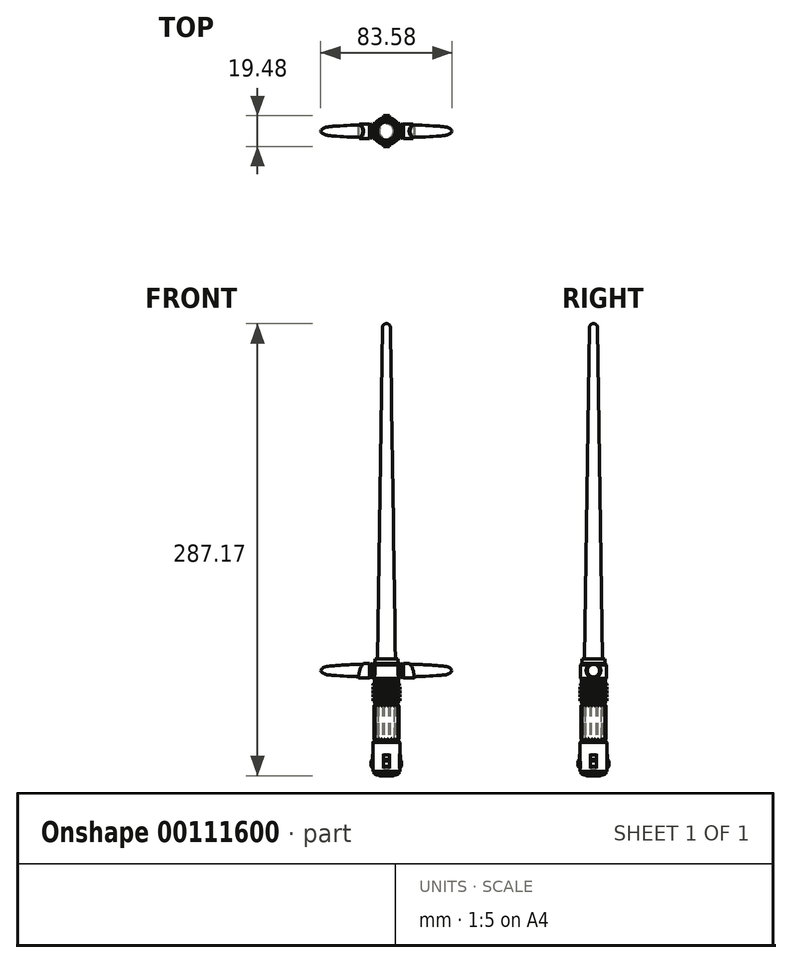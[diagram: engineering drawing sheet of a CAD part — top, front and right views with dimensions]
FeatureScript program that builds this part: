
annotation { "Feature Type Name" : "Feature", "Feature Type Description" : "" }
export const myFeature = defineFeature(function(context is Context, id is Id, definition is map)
    precondition{}
    {
        {
            var Q0;
            Q0=qCreatedBy(makeId("Front.planeOp"),FACE);
            var sketch = newSketch(context, id + "F0", { "sketchPlane" : qUnion([Q0])});
            skLineSegment(sketch, "E0", {"start": v(0, 37) * mm, "end": v(7.3, 37) * mm});
            skLineSegment(sketch, "E1", {"start": v(7.3, 37) * mm, "end": v(7.35, 34.29) * mm});
            skLineSegment(sketch, "E2", {"start": v(7.35, 34.29) * mm, "end": v(8.24, 33.16) * mm});
            skLineSegment(sketch, "E3", {"start": v(8.24, 33.16) * mm, "end": v(8.24, 24.6) * mm});
            skLineSegment(sketch, "E4", {"start": v(8.24, 24.6) * mm, "end": v(7.65, 23.84) * mm});
            skLineSegment(sketch, "E5", {"start": v(7.65, 23.84) * mm, "end": v(7.65, 21.71) * mm});
            skLineSegment(sketch, "E6", {"start": v(7.65, 21.71) * mm, "end": v(8.41, 21.12) * mm});
            skLineSegment(sketch, "E7", {"start": v(8.41, 21.12) * mm, "end": v(8.41, 20.12) * mm});
            skLineSegment(sketch, "E8", {"start": v(8.41, 20.12) * mm, "end": v(7.59, 20.12) * mm});
            skLineSegment(sketch, "E9", {"start": v(7.59, 20.12) * mm, "end": v(7.59, 19.18) * mm});
            skLineSegment(sketch, "E10", {"start": v(7.59, 19.18) * mm, "end": v(8.49, 19.18) * mm});
            skLineSegment(sketch, "E11", {"start": v(8.49, 19.18) * mm, "end": v(8.49, 17.5) * mm});
            skLineSegment(sketch, "E12", {"start": v(8.49, 17.5) * mm, "end": v(7.52, 17.5) * mm});
            skLineSegment(sketch, "E13", {"start": v(7.52, 17.5) * mm, "end": v(7.52, 16.91) * mm});
            skLineSegment(sketch, "E14", {"start": v(7.52, 16.91) * mm, "end": v(8.5, 16.91) * mm});
            skLineSegment(sketch, "E15", {"start": v(8.5, 16.91) * mm, "end": v(8.5, 15.12) * mm});
            skLineSegment(sketch, "E16", {"start": v(8.5, 15.12) * mm, "end": v(7.53, 15.12) * mm});
            skLineSegment(sketch, "E17", {"start": v(7.53, 15.12) * mm, "end": v(7.53, 14.37) * mm});
            skLineSegment(sketch, "E18", {"start": v(7.53, 14.37) * mm, "end": v(8.5, 14.37) * mm});
            skLineSegment(sketch, "E19", {"start": v(8.5, 14.37) * mm, "end": v(8.5, 12.85) * mm});
            skLineSegment(sketch, "E20", {"start": v(8.5, 12.85) * mm, "end": v(7.56, 12.85) * mm});
            skLineSegment(sketch, "E21", {"start": v(7.56, 12.85) * mm, "end": v(7.56, 11.91) * mm});
            skLineSegment(sketch, "E22", {"start": v(7.56, 11.91) * mm, "end": v(8.49, 11.91) * mm});
            skLineSegment(sketch, "E23", {"start": v(8.49, 11.91) * mm, "end": v(8.49, 10.4) * mm});
            skLineSegment(sketch, "E24", {"start": v(8.49, 10.4) * mm, "end": v(7.62, 10.4) * mm});
            skLineSegment(sketch, "E25", {"start": v(7.62, 10.4) * mm, "end": v(7.62, 9) * mm});
            skLineSegment(sketch, "E26", {"start": v(7.62, 9) * mm, "end": v(6.87, 9) * mm});
            skLineSegment(sketch, "E27", {"start": v(6.87, 9) * mm, "end": v(6.87, 8.81) * mm});
            skLineSegment(sketch, "E28", {"start": v(6.87, 8.81) * mm, "end": v(7.19, 8.81) * mm});
            skLineSegment(sketch, "E29", {"start": v(7.19, 8.81) * mm, "end": v(7.19, 8.55) * mm});
            skLineSegment(sketch, "E30", {"start": v(7.19, 8.55) * mm, "end": v(7.37, 8.55) * mm});
            skLineSegment(sketch, "E31", {"start": v(7.37, 8.55) * mm, "end": v(7.37, 7.87) * mm});
            skLineSegment(sketch, "E32", {"start": v(7.37, 7.87) * mm, "end": v(7.56, 7.87) * mm});
            skLineSegment(sketch, "E33", {"start": v(7.56, 7.87) * mm, "end": v(7.56, -14.92) * mm});
            skLineSegment(sketch, "E34", {"start": v(7.56, -14.92) * mm, "end": v(8.66, -16.09) * mm});
            skLineSegment(sketch, "E35", {"start": v(8.66, -16.09) * mm, "end": v(8.66, -23.38) * mm});
            skLineSegment(sketch, "E36", {"start": v(8.6, -32.9) * mm, "end": v(8.6, -34.53) * mm});
            skLineSegment(sketch, "E37", {"start": v(8.6, -34.53) * mm, "end": v(8.02, -34.53) * mm});
            skLineSegment(sketch, "E38", {"start": v(8.02, -34.53) * mm, "end": v(8.02, -35.87) * mm});
            skLineSegment(sketch, "E39", {"start": v(8.02, -35.87) * mm, "end": v(7.3, -35.87) * mm});
            skLineSegment(sketch, "E40", {"start": v(7.3, -35.87) * mm, "end": v(7.3, -36.2) * mm});
            skLineSegment(sketch, "E41", {"start": v(7.3, -36.2) * mm, "end": v(6.77, -36.2) * mm});
            skLineSegment(sketch, "E42", {"start": v(6.77, -36.2) * mm, "end": v(6.77, -36.42) * mm});
            skLineSegment(sketch, "E43", {"start": v(6.77, -36.42) * mm, "end": v(6.4, -36.42) * mm});
            skLineSegment(sketch, "E44", {"start": v(6.4, -36.42) * mm, "end": v(6.4, -36.76) * mm});
            skLineSegment(sketch, "E45", {"start": v(6.4, -36.76) * mm, "end": v(5.1, -36.76) * mm});
            skLineSegment(sketch, "E46", {"start": v(5.1, -36.76) * mm, "end": v(5.1, -36.92) * mm});
            skLineSegment(sketch, "E47", {"start": v(5.1, -36.92) * mm, "end": v(4.54, -36.92) * mm});
            skLineSegment(sketch, "E48", {"start": v(4.54, -36.92) * mm, "end": v(4.54, -37.17) * mm});
            skLineSegment(sketch, "E49", {"start": v(4.54, -37.17) * mm, "end": v(0, -37.17) * mm});
            skLineSegment(sketch, "E50", {"start": v(0, -37.17) * mm, "end": v(0, 37) * mm});
            skLineSegment(sketch, "E51", {"start": v(8.66, -23.38) * mm, "end": v(8.6, -32.9) * mm});
            skLineSegment(sketch, "E52", {"start": v(7.56, 7.87) * mm, "end": v(8.1, 7.39) * mm});
            skLineSegment(sketch, "E53", {"start": v(8.1, 7.39) * mm, "end": v(8.1, -14.41) * mm});
            skLineSegment(sketch, "E54", {"start": v(8.1, -14.41) * mm, "end": v(6.71, -14.41) * mm});
            skLineSegment(sketch, "E55", {"start": v(6.71, -14.41) * mm, "end": v(6.71, 7.86) * mm});
            skLineSegment(sketch, "E56", {"start": v(6.71, 7.86) * mm, "end": v(7.56, 7.87) * mm});
            skLineSegment(sketch, "E57", {"start": v(8.66, -23.38) * mm, "end": v(9.19, -24.01) * mm});
            skLineSegment(sketch, "E58", {"start": v(9.19, -24.01) * mm, "end": v(9.19, -26.92) * mm});
            skLineSegment(sketch, "E59", {"start": v(9.19, -26.92) * mm, "end": v(9.94, -27.8) * mm});
            skLineSegment(sketch, "E60", {"start": v(9.94, -27.8) * mm, "end": v(9.94, -31.32) * mm});
            skLineSegment(sketch, "E61", {"start": v(9.94, -31.32) * mm, "end": v(8.6, -32.4) * mm});
            skLineSegment(sketch, "E62", {"start": v(8.6, -32.4) * mm, "end": v(7.88, -32.4) * mm});
            skLineSegment(sketch, "E63", {"start": v(7.88, -32.4) * mm, "end": v(7.88, -23.67) * mm});
            skLineSegment(sketch, "E64", {"start": v(8.66, -23.38) * mm, "end": v(7.88, -23.38) * mm});
            skLineSegment(sketch, "E65", {"start": v(7.88, -23.38) * mm, "end": v(7.88, -23.67) * mm});
            skLineSegment(sketch, "E66", {"start": v(7.02, 33.16) * mm, "end": v(8.24, 33.16) * mm});
            skLineSegment(sketch, "E67", {"start": v(8.24, 33.16) * mm, "end": v(8.24, 34.28) * mm});
            skLineSegment(sketch, "E68", {"start": v(8.24, 34.28) * mm, "end": v(9.65, 34.28) * mm});
            skLineSegment(sketch, "E69", {"start": v(9.65, 34.28) * mm, "end": v(9.63, 33.97) * mm});
            skLineSegment(sketch, "E70", {"start": v(11.77, 34.18) * mm, "end": v(18.79, 34.18) * mm});
            skLineSegment(sketch, "E71", {"start": v(18.79, 34.18) * mm, "end": v(18.79, 29.6) * mm});
            skLineSegment(sketch, "E72", {"start": v(18.79, 29.6) * mm, "end": v(7.02, 29.6) * mm});
            skLineSegment(sketch, "E73", {"start": v(7.02, 29.6) * mm, "end": v(7.02, 33.16) * mm});
            skLineSegment(sketch, "E74", {"start": v(9.63, 33.97) * mm, "end": v(9.63, 33.3) * mm});
            skLineSegment(sketch, "E75", {"start": v(9.63, 33.3) * mm, "end": v(9.96, 33.3) * mm});
            skLineSegment(sketch, "E76", {"start": v(9.96, 33.3) * mm, "end": v(10.32, 33.78) * mm});
            skLineSegment(sketch, "E77", {"start": v(11.02, 33.88) * mm, "end": v(11.36, 33.63) * mm});
            skLineSegment(sketch, "E78", {"start": v(11.36, 33.63) * mm, "end": v(11.77, 34.18) * mm});
            skPoint(sketch, "E79.visualSharp", {"position": v(10.62, 34.18) * mm});
            skArc(sketch, "E79.filletArc", {"start": v(11.02, 33.88) * mm, "mid": v(10.65, 33.98) * mm, "end": v(10.32, 33.78) * mm});
            skPoint(sketch, "E80.endSnap0", {"position": v(12.9, 29.6) * mm});
            skLineSegment(sketch, "E81", {"start": v(48.79, 29.6) * mm, "end": v(18.79, 29.6) * mm});
            skPoint(sketch, "E82.3.internal.snap0", {"position": v(18.79, 31.9) * mm});
            skFitSpline(sketch, "E83", {"points": [v(15.28, 34.18) * mm, v(18.79, 33.79) * mm, v(29.96, 33.34) * mm, v(40.36, 32.7) * mm, v(46.93, 31.51) * mm, v(48.79, 29.6) * mm], "startDerivative": vector(18.62, -2.48) * mm, "endDerivative": vector(9.66, -15.82) * mm});
            skSolve(sketch);
        }
        {
            var Q0;
            Q0=makeQuery(id+"F0.imprint","IMPRINT",FACE,{"disambiguationData":[TD([[makeQuery(id+"F0.imprint","IMPRINT",EDGE,{"derivedFrom":sQuery(id+"F0.wireOp",EDGE,"E0")}),-1.0]])]});
            var Q1;
            {var subQ0=sQuery(id+"F0.wireOp",EDGE,"E66");Q1=makeQuery(id+"F0.imprint","IMPRINT",FACE,{"disambiguationData":[TD([[makeQuery(id+"F0.imprint","IMPRINT",EDGE,{"derivedFrom":subQ0}),-1.0]])]});}
            var Q2;
            {var subQ4=sQuery(id+"F0.wireOp",EDGE,"E55");Q2=makeQuery(id+"F0.imprint","IMPRINT",FACE,{"disambiguationData":[TD([[makeQuery(id+"F0.imprint","IMPRINT",EDGE,{"derivedFrom":subQ4}),-1.0]])]});}
            var Q3;
            {var subQ1=sQuery(id+"F0.wireOp",EDGE,"E62");Q3=makeQuery(id+"F0.imprint","IMPRINT",FACE,{"disambiguationData":[TD([[makeQuery(id+"F0.imprint","IMPRINT",EDGE,{"derivedFrom":subQ1}),-1.0]])]});}
            var Q4;
            Q4=sQuery(id+"F0.wireOp",EDGE,"E50");
            revolve(context, id + "F1", {"entities" : qUnion([Q0, Q1, Q2, Q3]), "axis" : qUnion([Q4]), "revolveType" : RevolveType.FULL});
        }
        {
            var Q0;
            {var subQ10=sQuery(id+"F0.wireOp",EDGE,"E67");Q0=makeQuery(id+"F0.imprint","IMPRINT",FACE,{"disambiguationData":[TD([[makeQuery(id+"F0.imprint","IMPRINT",EDGE,{"derivedFrom":subQ10}),-1.0]])]});}
            var Q1;
            {var subQ0=sQuery(id+"F0.wireOp",EDGE,"E71");var subQ1=sQuery(id+"F0.wireOp",EDGE,"E70");var subQ2=makeQuery(id+"F0.imprint","INTERSECT",VERTEX,{"derivedFrom":[subQ1,subQ0]});Q1=makeQuery(id+"F0.imprint","IMPRINT",FACE,{"disambiguationData":[TD([[makeQuery(id+"F0.imprint","IMPRINT",EDGE,{"disambiguationData":[TD([[subQ2,1.0]])],"derivedFrom":subQ1}),-1.0]])]});}
            var Q2;
            Q2=sQuery(id+"F0.wireOp",EDGE,"E72");
            revolve(context, id + "F2", {"entities" : qUnion([Q0, Q1]), "axis" : qUnion([Q2]), "revolveType" : RevolveType.FULL});
        }
        {
            var Q0;
            {var subQ0=sQuery(id+"F0.wireOp",EDGE,"E52");Q0=makeQuery(id+"F0.imprint","IMPRINT",FACE,{"disambiguationData":[TD([[makeQuery(id+"F0.imprint","IMPRINT",EDGE,{"derivedFrom":subQ0}),-1.0]])]});}
            extrude(context, id + "F3", {"entities" : qUnion([Q0]), "endBound" : BoundingType.SYMMETRIC, "depth" : 3 * mm});
        }
        {
            var Q0;
            {var subQ0=sQuery(id+"F0.wireOp",EDGE,"E57");Q0=makeQuery(id+"F0.imprint","IMPRINT",FACE,{"disambiguationData":[TD([[makeQuery(id+"F0.imprint","IMPRINT",EDGE,{"derivedFrom":subQ0}),-1.0]])]});}
            extrude(context, id + "F4", {"entities" : qUnion([Q0]), "endBound" : BoundingType.SYMMETRIC, "depth" : 4 * mm});
        }
        {
            var Q0;
            Q0=makeQuery(id+"F2.opRevolve","SWEPT_BODY",BODY,{"disambiguationData":[OSD([sQuery(id+"F0.wireOp",EDGE,"E3"),sQuery(id+"F0.wireOp",EDGE,"E67"),sQuery(id+"F0.wireOp",EDGE,"E68"),sQuery(id+"F0.wireOp",EDGE,"E69"),sQuery(id+"F0.wireOp",EDGE,"E70"),sQuery(id+"F0.wireOp",EDGE,"E71"),sQuery(id+"F0.wireOp",EDGE,"E72"),sQuery(id+"F0.wireOp",EDGE,"E74"),sQuery(id+"F0.wireOp",EDGE,"E75"),sQuery(id+"F0.wireOp",EDGE,"E76")])]});
            var Q1;
            Q1=sQuery(id+"F0.wireOp",EDGE,"E72");
            var Q2;
            Q2=sQuery(id+"F0.wireOp",EDGE,"E72");
            transform(context, id + "F5", {"entities" : qUnion([Q0]), "transformType" : TransformType.TRANSLATION_DISTANCE, "transformDirection" : qUnion([Q2]), "distance" : 1 * mm, "makeCopy" : false});
        }
        {
            var Q0;
            Q0=makeQuery(id+"F3.opExtrude","SWEPT_BODY",BODY,{"disambiguationData":[OSD([sQuery(id+"F0.wireOp",EDGE,"E33"),sQuery(id+"F0.wireOp",EDGE,"E52"),sQuery(id+"F0.wireOp",EDGE,"E53"),sQuery(id+"F0.wireOp",EDGE,"E54")])]});
            var Q1;
            Q1=sQuery(id+"F0.wireOp",EDGE,"E54");
            var Q2;
            Q2=sQuery(id+"F0.wireOp",EDGE,"E54");
            transform(context, id + "F6", {"entities" : qUnion([Q0]), "transformType" : TransformType.TRANSLATION_DISTANCE, "transformDirection" : qUnion([Q2]), "distance" : 0.2 * mm, "makeCopy" : false});
        }
        {
            var Q0;
            Q0=makeQuery(id+"F4.opExtrude","SWEPT_BODY",BODY,{"disambiguationData":[OSD([sQuery(id+"F0.wireOp",EDGE,"E51"),sQuery(id+"F0.wireOp",EDGE,"E57"),sQuery(id+"F0.wireOp",EDGE,"E58"),sQuery(id+"F0.wireOp",EDGE,"E59"),sQuery(id+"F0.wireOp",EDGE,"E60"),sQuery(id+"F0.wireOp",EDGE,"E61")])]});
            var Q1;
            Q1=sQuery(id+"F0.wireOp",EDGE,"E54");
            transform(context, id + "F7", {"entities" : qUnion([Q0]), "transformType" : TransformType.TRANSLATION_DISTANCE, "transformDirection" : qUnion([Q1]), "distance" : 0.2 * mm, "makeCopy" : false});
        }
        {
            var Q0;
            Q0=makeQuery(id+"F2.opRevolve","SWEPT_BODY",BODY,{"disambiguationData":[OSD([sQuery(id+"F0.wireOp",EDGE,"E3"),sQuery(id+"F0.wireOp",EDGE,"E67"),sQuery(id+"F0.wireOp",EDGE,"E68"),sQuery(id+"F0.wireOp",EDGE,"E69"),sQuery(id+"F0.wireOp",EDGE,"E70"),sQuery(id+"F0.wireOp",EDGE,"E71"),sQuery(id+"F0.wireOp",EDGE,"E72"),sQuery(id+"F0.wireOp",EDGE,"E74"),sQuery(id+"F0.wireOp",EDGE,"E75"),sQuery(id+"F0.wireOp",EDGE,"E76")])]});
            var Q1;
            Q1=qCreatedBy(makeId("Right.planeOp"),FACE);
            mirror(context, id + "F8", {"operationType" : NewBodyOperationType.ADD, "entities" : qUnion([Q0]), "mirrorPlane" : qUnion([Q1])});
        }
        {
            var Q0;
            Q0=makeQuery(id+"F3.opExtrude","SWEPT_FACE",FACE,{"disambiguationData":[OSD([sQuery(id+"F0.wireOp",EDGE,"E53")])]});
            fillet(context, id + "F9", {"entities" : qUnion([Q0]), "radius" : 1 * mm, "tangentPropagation" : true, "allowEdgeOverflow" : false});
        }
        {
            var Q0;
            Q0=makeQuery(id+"F3.opExtrude","SWEPT_BODY",BODY,{"disambiguationData":[OSD([sQuery(id+"F0.wireOp",EDGE,"E33"),sQuery(id+"F0.wireOp",EDGE,"E52"),sQuery(id+"F0.wireOp",EDGE,"E53"),sQuery(id+"F0.wireOp",EDGE,"E54")])]});
            var Q1;
            Q1=sQuery(id+"F0.wireOp",EDGE,"E50");
            circularPattern(context, id + "F10", {"entities" : qUnion([Q0]), "axis" : qUnion([Q1]), "angle" : 30 * degree, "instanceCount" : 12});
        }
        {
            var Q0;
            Q0=makeQuery(id+"F4.opExtrude","SWEPT_BODY",BODY,{"disambiguationData":[OSD([sQuery(id+"F0.wireOp",EDGE,"E51"),sQuery(id+"F0.wireOp",EDGE,"E57"),sQuery(id+"F0.wireOp",EDGE,"E58"),sQuery(id+"F0.wireOp",EDGE,"E59"),sQuery(id+"F0.wireOp",EDGE,"E60"),sQuery(id+"F0.wireOp",EDGE,"E61")])]});
            var Q1;
            Q1=sQuery(id+"F0.wireOp",EDGE,"E50");
            circularPattern(context, id + "F11", {"entities" : qUnion([Q0]), "axis" : qUnion([Q1]), "angle" : 90 * degree, "instanceCount" : 4});
        }
        {
            var Q0;
            Q0=qCreatedBy(makeId("Front.planeOp"),FACE);
            var sketch = newSketch(context, id + "F12", { "sketchPlane" : qUnion([Q0])});
            skLineSegment(sketch, "E84", {"start": v(17.79, 34.9) * mm, "end": v(13.44, 34.9) * mm});
            skLineSegment(sketch, "E85", {"start": v(17.79, 34.9) * mm, "end": v(17.79, 24.36) * mm});
            skFitSpline(sketch, "E86", {"points": [v(13.44, 34.9) * mm, v(15.9, 32.37) * mm, v(17.37, 28.19) * mm, v(17.79, 24.36) * mm], "startDerivative": vector(9.05, -4.4) * mm, "endDerivative": vector(0.82, -10.85) * mm});
            skLineSegment(sketch, "E87.MirrorCS", {"start": v(-17.79, 34.9) * mm, "end": v(-17.79, 24.36) * mm});
            skLineSegment(sketch, "E88.MirrorCS", {"start": v(-17.79, 34.9) * mm, "end": v(-13.44, 34.9) * mm});
            skFitSpline(sketch, "E89.MirrorCS", {"points": [v(-13.44, 34.9) * mm, v(-15.9, 32.37) * mm, v(-17.37, 28.19) * mm, v(-17.79, 24.36) * mm], "startDerivative": vector(-9.05, -4.4) * mm, "endDerivative": vector(-0.82, -10.85) * mm});
            skSolve(sketch);
        }
        {
            var Q0;
            Q0 = qSketchRegion(id + "F12", true);
            extrude(context, id + "F13", {"entities" : qUnion([Q0]), "operationType" : NewBodyOperationType.REMOVE, "endBound" : BoundingType.SYMMETRIC, "oppositeDirection" : true, "depth" : 50 * mm});
        }
        {
            var Q0;
            Q0=makeQuery(id+"F1.opRevolve","SWEPT_FACE",FACE,{"disambiguationData":[OSD([sQuery(id+"F0.wireOp",EDGE,"E0")])]});
            var sketch = newSketch(context, id + "F14", { "sketchPlane" : qUnion([Q0])});
            skCircle(sketch, "E90", {"center": v(0, 0) * mm, "radius": 5.75 * mm});
            skSolve(sketch);
        }
        {
            var Q0;
            Q0=qCreatedBy(makeId("Top.planeOp"),FACE);
            cPlane(context, id + "F15", {"entities" : qUnion([Q0]), "cplaneType" : CPlaneType.OFFSET, "offset" : 250 * mm, "width" : 150 * mm, "height" : 150 * mm});
        }
        {
            var Q0;
            Q0=qCreatedBy(id+"F15.planeOp",FACE);
            var sketch = newSketch(context, id + "F16", { "sketchPlane" : qUnion([Q0])});
            skCircle(sketch, "E91", {"center": v(0, 0) * mm, "radius": 2.5 * mm});
            skSolve(sketch);
        }
        {
            var Q1;
            Q1 = qSketchRegion(id + "F16", true);
            var Q2;
            Q2 = qSketchRegion(id + "F14", true);
            loft(context, id + "F17", {"operationType" : NewBodyOperationType.ADD, "sheetProfilesArray" : [{ "sheetProfileEntities" : qUnion([Q1]) }, { "sheetProfileEntities" : qUnion([Q2]) }]});
        }
        {
            var Q0;
            Q0=makeQuery(id+"F17.opLoft","CAP_FACE",FACE,{"disambiguationData":[OSD([makeQuery(id+"F16.imprint","IMPRINT",FACE,{"disambiguationData":[TD([[makeQuery(id+"F16.imprint","IMPRINT",EDGE,{"derivedFrom":sQuery(id+"F16.wireOp",EDGE,"E91")}),1.0]])]})])],"isStart":true});
            fillet(context, id + "F18", {"entities" : qUnion([Q0]), "radius" : 2.5 * mm, "tangentPropagation" : true, "allowEdgeOverflow" : false});
        }
        {
            var Q0;
            {var subQ0=sQuery(id+"F0.wireOp",EDGE,"E81");Q0=makeQuery(id+"F0.imprint","IMPRINT",FACE,{"disambiguationData":[TD([[makeQuery(id+"F0.imprint","IMPRINT",EDGE,{"derivedFrom":subQ0}),-1.0]])]});}
            var Q1;
            Q1=sQuery(id+"F0.wireOp",EDGE,"E81");
            revolve(context, id + "F19", {"entities" : qUnion([Q0]), "axis" : qUnion([Q1]), "revolveType" : RevolveType.FULL});
        }
        {
            var Q0;
            Q0=makeQuery(id+"F19.opRevolve","SWEPT_BODY",BODY,{"disambiguationData":[OSD([sQuery(id+"F0.wireOp",EDGE,"E71"),sQuery(id+"F0.wireOp",EDGE,"E81"),sQuery(id+"F0.wireOp",EDGE,"E83")])]});
            var Q1;
            Q1=sQuery(id+"F0.wireOp",EDGE,"E81");
            var Q2;
            Q2=sQuery(id+"F0.wireOp",EDGE,"E81");
            transform(context, id + "F20", {"entities" : qUnion([Q0]), "transformType" : TransformType.TRANSLATION_DISTANCE, "transformDirection" : qUnion([Q2]), "distance" : 7 * mm, "makeCopy" : false});
        }
        {
            var Q0;
            Q0=makeQuery(id+"F19.opRevolve","SWEPT_BODY",BODY,{"disambiguationData":[OSD([sQuery(id+"F0.wireOp",EDGE,"E71"),sQuery(id+"F0.wireOp",EDGE,"E81"),sQuery(id+"F0.wireOp",EDGE,"E83")])]});
            var Q1;
            Q1=qCreatedBy(makeId("Right.planeOp"),FACE);
            mirror(context, id + "F21", {"operationType" : NewBodyOperationType.ADD, "entities" : qUnion([Q0]), "mirrorPlane" : qUnion([Q1])});
        }
    });
